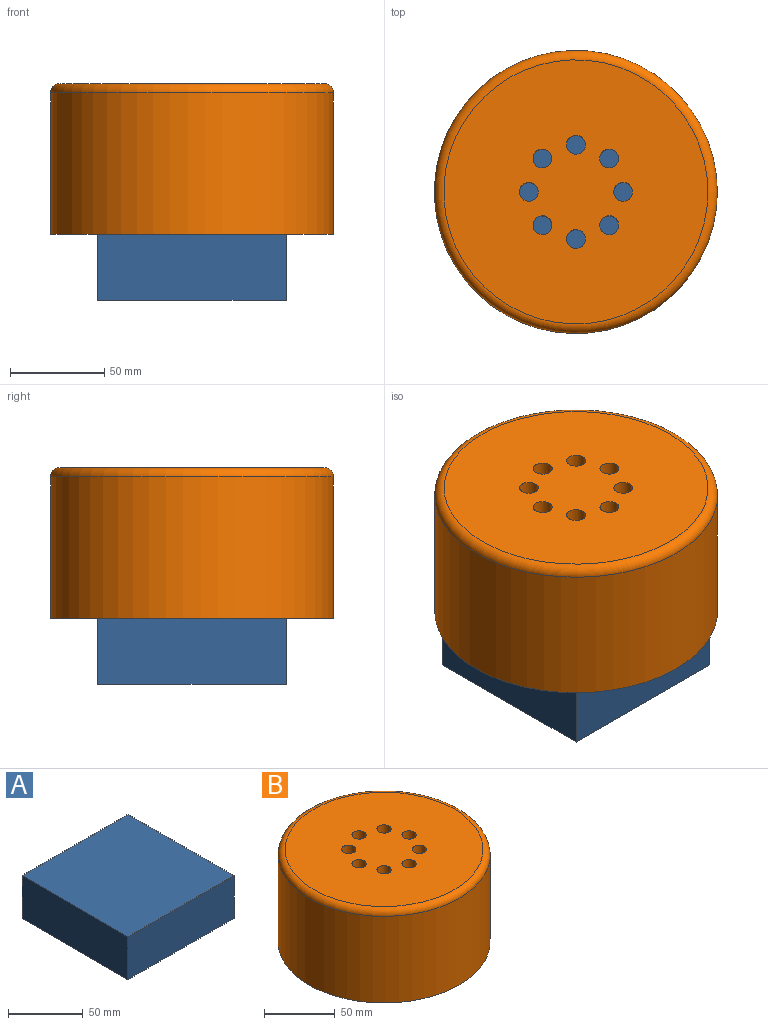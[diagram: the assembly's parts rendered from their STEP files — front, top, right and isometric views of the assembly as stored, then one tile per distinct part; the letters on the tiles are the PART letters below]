
ASSEMBLY  parts=2 mates=1
PART A: 6 faces, bbox 100x100x35 mm
  f0: plane 100x35mm, normal (0,1,0), area 3500mm2, adj f1,f3,f4,f5
  f1: plane 100x35mm, normal (-1,0,0), area 3500mm2, adj f0,f2,f4,f5
  f2: plane 100x35mm, normal (0,-1,0), area 3500mm2, adj f1,f3,f4,f5
  f3: plane 100x35mm, normal (1,0,0), area 3500mm2, adj f0,f2,f4,f5
  f4: plane 100x100mm, normal (0,0,-1), area 10000mm2, adj f0,f1,f2,f3
  f5: plane 100x100mm, normal (0,0,1), area 10000mm2, adj f0,f1,f2,f3
PART B: 12 faces, bbox 162.4x162.4x80 mm
  f0: cylinder r=75mm len=150mm, axis (0,0,-1), area 35342.9mm2, adj f2,f3
  f1: plane 140x140mm, normal (0,0,1), area 14765.5mm2, adj f3,f4,f5,f6,f7,f8,f9,f10
  f2: plane 150x150mm, normal (0,0,-1), area 17043.1mm2, adj f0,f4,f5,f6,f7,f8,f9,f10
  f3: torus R=70mm, axis (0,0,1), area 3611.4mm2, adj f0,f1
  f4: cylinder r=5mm len=80mm, axis (0,0,1), area 2513.3mm2, adj f1,f2
  f5: cylinder r=5mm len=80mm, axis (0,0,1), area 2513.3mm2, adj f1,f2
  f6: cylinder r=5mm len=80mm, axis (0,0,1), area 2513.3mm2, adj f1,f2
  f7: cylinder r=5mm len=80mm, axis (0,0,1), area 2513.3mm2, adj f1,f2
  f8: cylinder r=5mm len=80mm, axis (0,0,1), area 2513.3mm2, adj f1,f2
  f9: cylinder r=5mm len=80mm, axis (0,0,1), area 2513.3mm2, adj f1,f2
  f10: cylinder r=5mm len=80mm, axis (0,0,1), area 2513.3mm2, adj f1,f2
  f11: cylinder r=5mm len=80mm, axis (0,0,1), area 2513.3mm2, adj f1,f2
PLACE A t=(141.53,94.81,37.14)mm
PLACE B t=(141.53,94.81,37.14)mm
MATE parallel B.f0 <-> A.f5  axis (0,0,-1) through (141.53,94.81,37.14)mm
